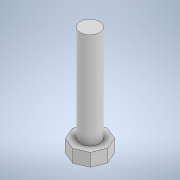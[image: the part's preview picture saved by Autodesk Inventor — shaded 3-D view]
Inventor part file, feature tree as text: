
AUTODESK INVENTOR PART (.ipt)
format: ipt  version: 2022 (Build 260153000, 153)  size: 105,984 bytes
history: native  units: in
note: dims shown in document units (in); Inventor stores cm internally (conversion verified against a paired STEP export)
features: extrude x2, sketch x2
ambient origin geometry x8: Origin, YZ Plane, XZ Plane, XY Plane, X Axis, Y Axis, Z Axis, Center Point
bodies: Solid1 (feature_tree)
feature tree (4):
  extrude  "Extrusion1"  Depth=0.0787in TaperAngle=0.0deg
  extrude  "Extrusion2"  Depth=0.5906in TaperAngle=0.0deg
  sketch  "Sketch1"  dims[d0=0.1969in d1=0.0787in d2=0.0in]
  sketch  "Sketch2"  dims[d3=0.1181in d4=0.5906in d5=0.0in]
